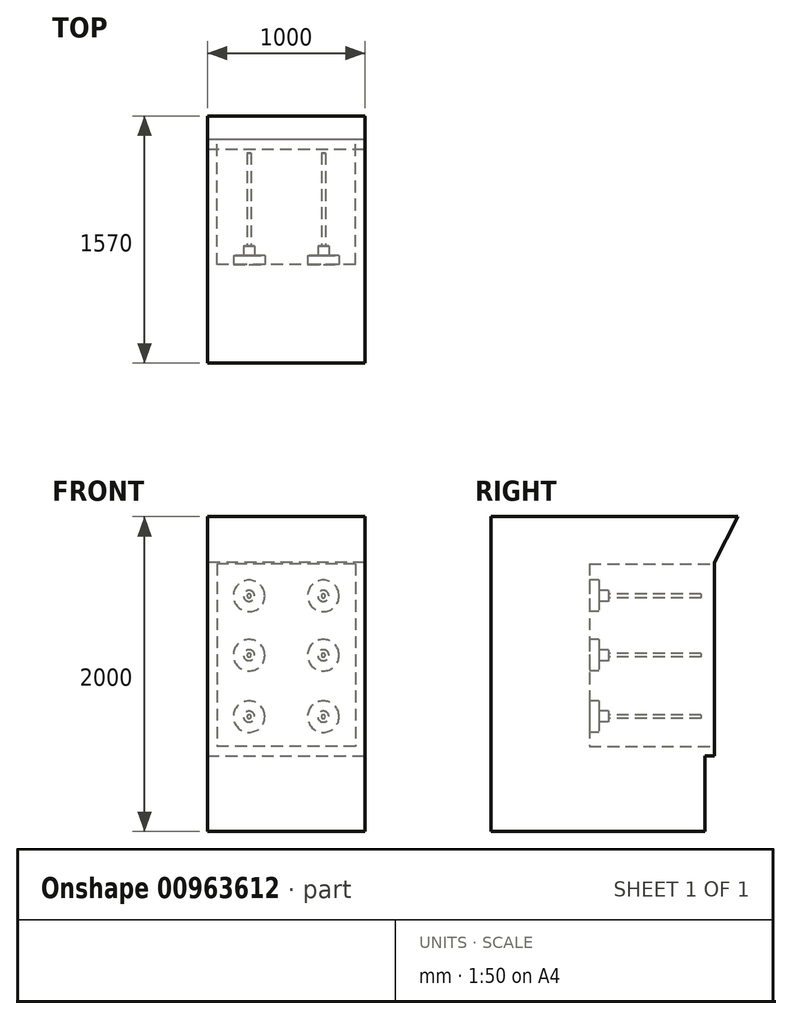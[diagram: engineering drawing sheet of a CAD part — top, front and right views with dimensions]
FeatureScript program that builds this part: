
annotation { "Feature Type Name" : "Feature", "Feature Type Description" : "" }
export const myFeature = defineFeature(function(context is Context, id is Id, definition is map)
    precondition{}
    {
        {
            var Q0;
            Q0=qCreatedBy(makeId("Right.planeOp"),FACE);
            var sketch = newSketch(context, id + "F0", { "sketchPlane" : qUnion([Q0])});
            skLineSegment(sketch, "E0.bottom", {"start": v(-710, 1000) * mm, "end": v(710, 1000) * mm});
            skLineSegment(sketch, "E0.top", {"start": v(-710, -1000) * mm, "end": v(650, -1000) * mm});
            skLineSegment(sketch, "E0.left", {"start": v(-710, 1000) * mm, "end": v(-710, -1000) * mm});
            skLineSegment(sketch, "E1", {"start": v(0, 1414.62) * mm, "end": v(0, -1265.15) * mm, "construction": true});
            skLineSegment(sketch, "E2", {"start": v(-1520.01, 0) * mm, "end": v(1358.5, 0) * mm, "construction": true});
            skLineSegment(sketch, "E3", {"start": v(650, -1000) * mm, "end": v(650, -520) * mm});
            skLineSegment(sketch, "E4", {"start": v(650, -520) * mm, "end": v(710, -520) * mm});
            skLineSegment(sketch, "E5", {"start": v(710, -520) * mm, "end": v(710, 1000) * mm});
            skSolve(sketch);
        }
        {
            var Q0;
            Q0 = qSketchRegion(id + "F0", true);
            extrude(context, id + "F1", {"entities" : qUnion([Q0]), "oppositeDirection" : true, "depth" : 1000 * mm, "offsetDistance" : 25.4 * mm});
        }
        {
            var Q0;
            Q0=makeQuery(id+"F1.opExtrude","SWEPT_FACE",FACE,{"disambiguationData":[OSD([sQuery(id+"F0.wireOp",EDGE,"E5")])]});
            var sketch = newSketch(context, id + "F2", { "sketchPlane" : qUnion([Q0])});
            skLineSegment(sketch, "E6.bottom", {"start": v(60, 700) * mm, "end": v(940, 700) * mm});
            skLineSegment(sketch, "E6.top", {"start": v(60, -460) * mm, "end": v(940, -460) * mm});
            skLineSegment(sketch, "E6.left", {"start": v(60, 700) * mm, "end": v(60, -460) * mm});
            skLineSegment(sketch, "E6.right", {"start": v(940, 700) * mm, "end": v(940, -460) * mm});
            skSolve(sketch);
        }
        {
            var Q0;
            Q0 = qSketchRegion(id + "F2", true);
            extrude(context, id + "F3", {"entities" : qUnion([Q0]), "operationType" : NewBodyOperationType.REMOVE, "oppositeDirection" : true, "depth" : 795 * mm, "offsetDistance" : 25.4 * mm});
        }
        {
            var Q0;
            Q0=makeQuery(id+"F1.opExtrude","CAP_FACE",FACE,{"disambiguationData":[OSD([sQuery(id+"F0.wireOp",EDGE,"E0.bottom"),sQuery(id+"F0.wireOp",EDGE,"E0.top"),sQuery(id+"F0.wireOp",EDGE,"E0.left"),sQuery(id+"F0.wireOp",EDGE,"E3"),sQuery(id+"F0.wireOp",EDGE,"E4"),sQuery(id+"F0.wireOp",EDGE,"E5")])],"isStart":false});
            var sketch = newSketch(context, id + "F4", { "sketchPlane" : qUnion([Q0])});
            skLineSegment(sketch, "E7", {"start": v(-710, 1000) * mm, "end": v(-860, 1000) * mm});
            skLineSegment(sketch, "E8", {"start": v(-860, 1000) * mm, "end": v(-710, 710) * mm});
            skLineSegment(sketch, "E9", {"start": v(-710, 710) * mm, "end": v(-710, 1000) * mm});
            skSolve(sketch);
        }
        {
            var Q0;
            Q0 = qSketchRegion(id + "F4", true);
            var Q1;
            Q1=makeQuery(id+"F1.opExtrude","CAP_FACE",FACE,{"disambiguationData":[OSD([sQuery(id+"F0.wireOp",EDGE,"E0.bottom"),sQuery(id+"F0.wireOp",EDGE,"E0.top"),sQuery(id+"F0.wireOp",EDGE,"E0.left"),sQuery(id+"F0.wireOp",EDGE,"E3"),sQuery(id+"F0.wireOp",EDGE,"E4"),sQuery(id+"F0.wireOp",EDGE,"E5")])],"isStart":true});
            extrude(context, id + "F5", {"entities" : qUnion([Q0]), "operationType" : NewBodyOperationType.ADD, "endBound" : BoundingType.UP_TO_SURFACE, "oppositeDirection" : true, "depth" : 25.4 * mm, "endBoundEntityFace" : qUnion([Q1]), "offsetDistance" : 25.4 * mm});
        }
        {
            var Q0;
            Q0=makeQuery(id+"F3.boolean.opBoolean","COPY",FACE,{"derivedFrom":makeQuery(id+"F3.opExtrude","CAP_FACE",FACE,{"disambiguationData":[OSD([sQuery(id+"F2.wireOp",EDGE,"E6.bottom"),sQuery(id+"F2.wireOp",EDGE,"E6.top"),sQuery(id+"F2.wireOp",EDGE,"E6.left"),sQuery(id+"F2.wireOp",EDGE,"E6.right")])],"isStart":false})});
            var sketch = newSketch(context, id + "F6", { "sketchPlane" : qUnion([Q0])});
            skLineSegment(sketch, "E10", {"start": v(500, 700) * mm, "end": v(500, -460) * mm, "construction": true});
            skLineSegment(sketch, "E11", {"start": v(60, 120) * mm, "end": v(940, 120) * mm, "construction": true});
            skCircle(sketch, "E12", {"center": v(735.73, 496.75) * mm, "radius": 100 * mm});
            skCircle(sketch, "E13", {"center": v(735.73, 120) * mm, "radius": 100 * mm});
            skCircle(sketch, "E14", {"center": v(735.73, -270.27) * mm, "radius": 100 * mm});
            skCircle(sketch, "E15.MirrorC", {"center": v(264.27, 496.75) * mm, "radius": 100 * mm});
            skCircle(sketch, "E16.MirrorC", {"center": v(264.27, 120) * mm, "radius": 100 * mm});
            skCircle(sketch, "E17.MirrorC", {"center": v(264.27, -270.27) * mm, "radius": 100 * mm});
            skSolve(sketch);
        }
        {
            var Q0;
            Q0 = qSketchRegion(id + "F6", true);
            extrude(context, id + "F7", {"entities" : qUnion([Q0]), "operationType" : NewBodyOperationType.ADD, "depth" : 60 * mm, "offsetDistance" : 25.4 * mm});
        }
        {
            var Q0;
            Q0=makeQuery(id+"F7.opExtrude","CAP_FACE",FACE,{"disambiguationData":[OSD([sQuery(id+"F6.wireOp",EDGE,"E12")])],"isStart":false});
            var sketch = newSketch(context, id + "F8", { "sketchPlane" : qUnion([Q0])});
            skCircle(sketch, "E18", {"center": v(735.73, 496.75) * mm, "radius": 35 * mm});
            skCircle(sketch, "E19", {"center": v(735.73, 120) * mm, "radius": 35 * mm});
            skCircle(sketch, "E20", {"center": v(735.73, -270.27) * mm, "radius": 35 * mm});
            skCircle(sketch, "E21", {"center": v(264.27, -270.27) * mm, "radius": 35 * mm});
            skCircle(sketch, "E22", {"center": v(264.27, 120) * mm, "radius": 35 * mm});
            skCircle(sketch, "E23", {"center": v(264.27, 496.75) * mm, "radius": 35 * mm});
            skSolve(sketch);
        }
        {
            var Q0;
            Q0 = qSketchRegion(id + "F8", true);
            extrude(context, id + "F9", {"entities" : qUnion([Q0]), "operationType" : NewBodyOperationType.ADD, "depth" : 60 * mm, "offsetDistance" : 25.4 * mm});
        }
        {
            var Q0;
            Q0=makeQuery(id+"F9.opExtrude","CAP_FACE",FACE,{"disambiguationData":[OSD([sQuery(id+"F8.wireOp",EDGE,"E18")])],"isStart":false});
            var sketch = newSketch(context, id + "F10", { "sketchPlane" : qUnion([Q0])});
            skCircle(sketch, "E24", {"center": v(735.73, 496.75) * mm, "radius": 12.5 * mm});
            skCircle(sketch, "E25", {"center": v(735.73, 120) * mm, "radius": 12.5 * mm});
            skCircle(sketch, "E26", {"center": v(735.73, -270.27) * mm, "radius": 12.5 * mm});
            skCircle(sketch, "E27", {"center": v(264.27, -270.27) * mm, "radius": 12.5 * mm});
            skCircle(sketch, "E28", {"center": v(264.27, 120) * mm, "radius": 12.5 * mm});
            skCircle(sketch, "E29", {"center": v(264.27, 496.75) * mm, "radius": 12.5 * mm});
            skSolve(sketch);
        }
        {
            var Q0;
            Q0 = qSketchRegion(id + "F10", true);
            extrude(context, id + "F11", {"entities" : qUnion([Q0]), "operationType" : NewBodyOperationType.ADD, "depth" : 590 * mm, "offsetDistance" : 25.4 * mm});
        }
    });
